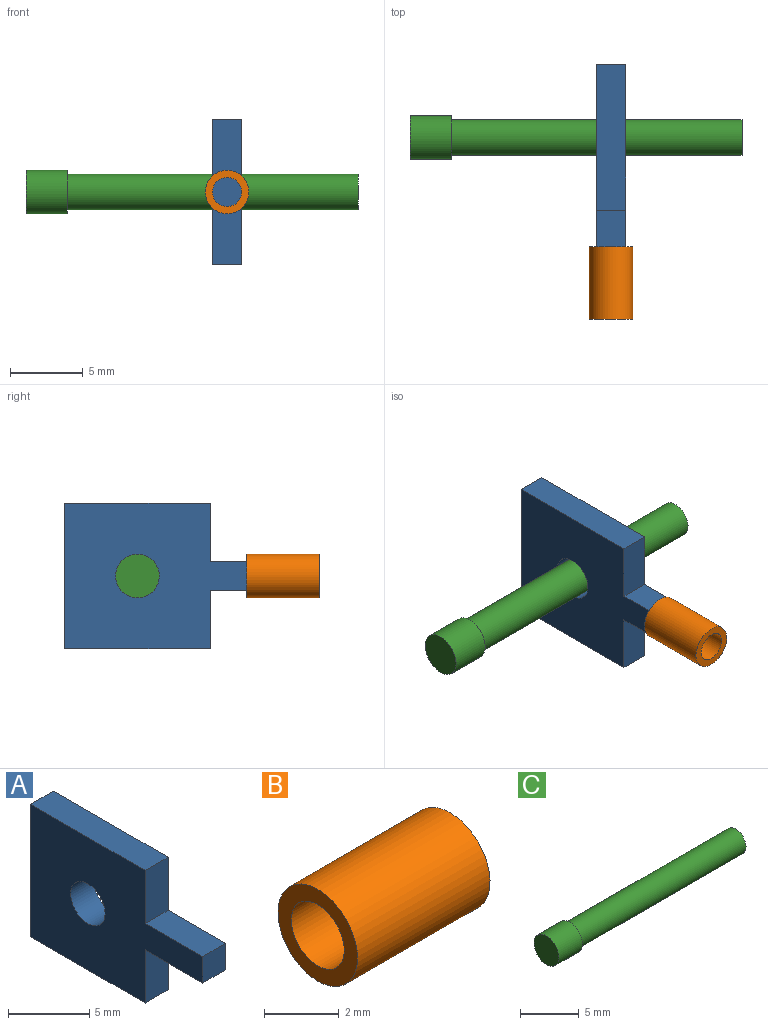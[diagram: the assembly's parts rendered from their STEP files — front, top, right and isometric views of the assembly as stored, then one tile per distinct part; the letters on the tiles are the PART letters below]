
ASSEMBLY  parts=3 mates=2
PART A: 11 faces, bbox 2x15x10 mm
  f0: plane 10x2mm, normal (0,0,1), area 20mm2, adj f1,f7,f9,f10
  f1: plane 4x2mm, normal (0,-1,0), area 8mm2, adj f0,f2,f9,f10
  f2: plane 5x2mm, normal (0,0,1), area 10mm2, adj f1,f3,f9,f10
  f3: plane 2x2mm, normal (0,-1,0), area 4mm2, adj f2,f4,f9,f10
  f4: plane 5x2mm, normal (0,0,-1), area 10mm2, adj f3,f5,f9,f10
  f5: plane 4x2mm, normal (0,-1,0), area 8mm2, adj f4,f6,f9,f10
  f6: plane 10x2mm, normal (0,0,-1), area 20mm2, adj f5,f7,f9,f10
  f7: plane 10x2mm, normal (0,1,0), area 20mm2, adj f0,f6,f9,f10
  f8: cylinder r=1.5mm len=3mm, axis (-1,0,0), area 18.8mm2, adj f9,f10
  f9: plane 15x10mm, normal (1,0,0), area 102.9mm2, adj f0,f1,f2,f3,f4,f5,f6,f7
  f10: plane 15x10mm, normal (-1,0,0), area 102.9mm2, adj f0,f1,f2,f3,f4,f5,f6,f7
PART B: 4 faces, bbox 5x3x3 mm
  f0: cylinder r=1mm len=5mm, axis (-1,0,0), area 31.4mm2, adj f2,f3
  f1: cylinder r=1.5mm len=5mm, axis (-1,0,0), area 47.1mm2, adj f2,f3
  f2: plane 3x3mm, normal (1,0,0), area 3.9mm2, adj f0,f1
  f3: plane 3x3mm, normal (-1,0,0), area 3.9mm2, adj f0,f1
PART C: 5 faces, bbox 22.8x3x3 mm
  f0: cylinder r=1.5mm len=3mm, axis (-1,0,0), area 26.7mm2, adj f1,f2
  f1: plane 3x3mm, normal (1,0,0), area 2.3mm2, adj f0,f3
  f2: plane 3x3mm, normal (-1,0,0), area 7.1mm2, adj f0
  f3: cylinder r=1.23mm len=20mm, axis (-1,0,0), area 154.5mm2, adj f1,f4
  f4: plane 2.46x2.46mm, normal (1,0,0), area 4.7mm2, adj f3
PLACE A t=(-5.25,-0.09,-0.21)mm
PLACE B rot(axis=(-0.58,-0.58,0.58),120deg) t=(-4.25,-12.59,-0.21)mm
PLACE C t=(-18.08,-0.09,-0.21)mm
MATE cylindrical C.f3 <-> A.f8  axis (-1,0,0) through (-5.25,-0.09,-0.21)mm
MATE cylindrical B.f0 <-> A.f3  axis (0,-1,0) through (-4.25,-10.09,-0.21)mm
